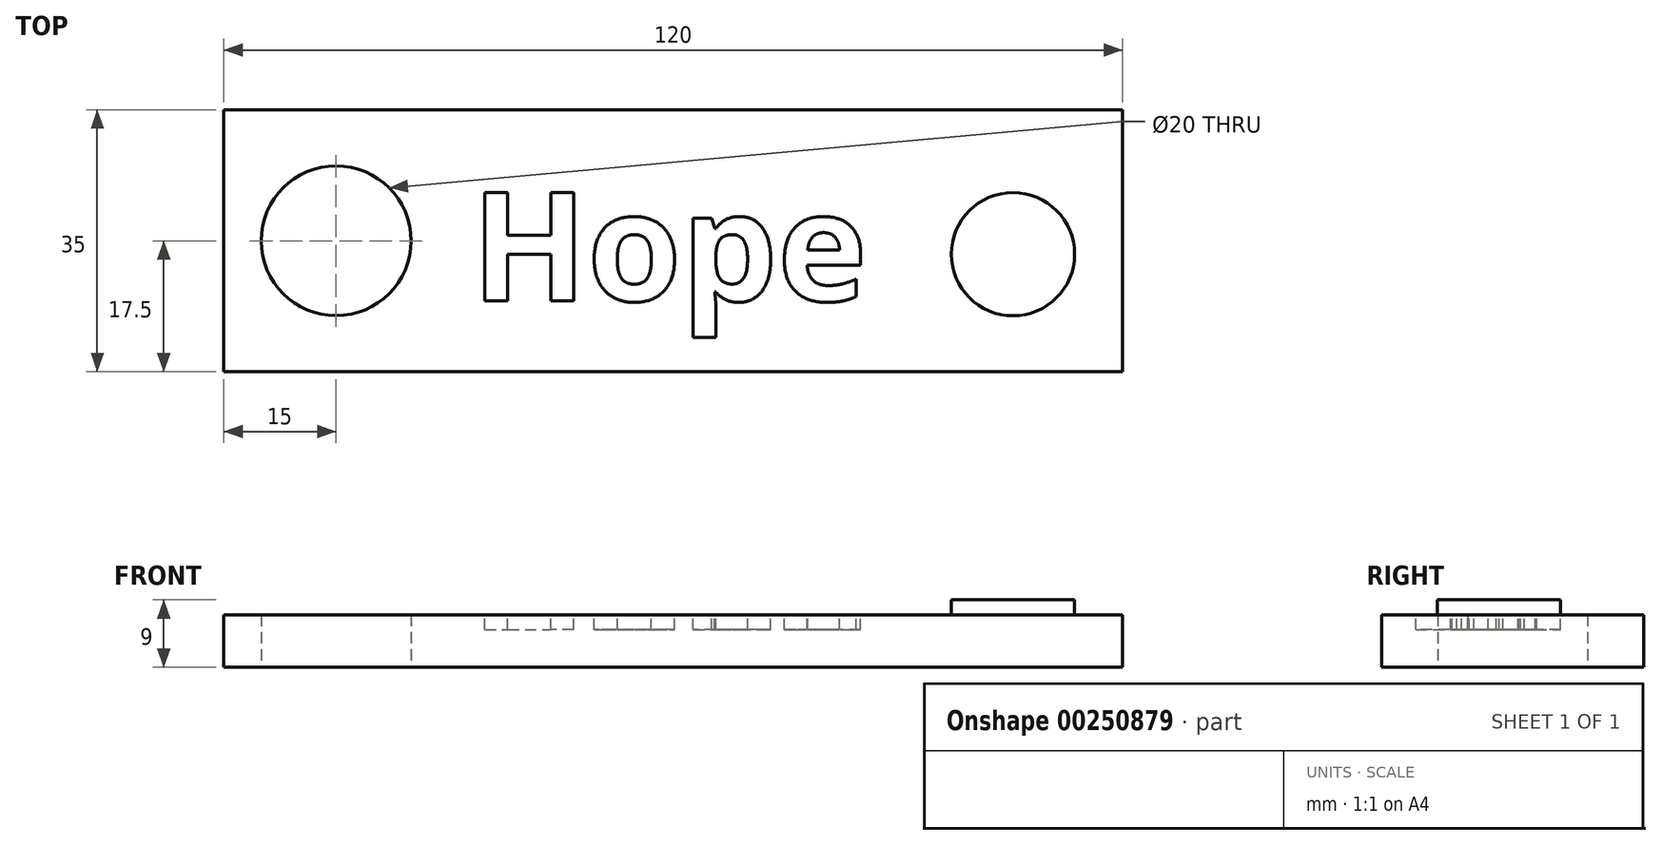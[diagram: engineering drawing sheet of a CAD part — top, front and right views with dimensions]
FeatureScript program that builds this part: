
annotation { "Feature Type Name" : "Feature", "Feature Type Description" : "" }
export const myFeature = defineFeature(function(context is Context, id is Id, definition is map)
    precondition{}
    {
        {
            var Q0;
            Q0=qCreatedBy(makeId("Top.planeOp"),FACE);
            var sketch = newSketch(context, id + "F0", { "sketchPlane" : qUnion([Q0])});
            skLineSegment(sketch, "E0.bottom", {"start": v(60, -17.5) * mm, "end": v(-60, -17.5) * mm});
            skLineSegment(sketch, "E0.top", {"start": v(60, 17.5) * mm, "end": v(-60, 17.5) * mm});
            skLineSegment(sketch, "E0.left", {"start": v(60, -17.5) * mm, "end": v(60, 17.5) * mm});
            skLineSegment(sketch, "E0.right", {"start": v(-60, -17.5) * mm, "end": v(-60, 17.5) * mm});
            skPoint(sketch, "E0.middle", {"position": v(0, 0) * mm});
            skCircle(sketch, "E1", {"center": v(-45, 0) * mm, "radius": 10 * mm});
            skSolve(sketch);
        }
        {
            var Q0;
            Q0=makeQuery(id+"F0.imprint","IMPRINT",FACE,{"disambiguationData":[TD([[makeQuery(id+"F0.imprint","IMPRINT",EDGE,{"derivedFrom":sQuery(id+"F0.wireOp",EDGE,"E0.bottom")}),-1.0]])]});
            var Q1;
            Q1=makeQuery(id+"FlfnzI0YaSvKUO7_0.imprint","IMPRINT",FACE,{"disambiguationData":[TD([[makeQuery(id+"FlfnzI0YaSvKUO7_0.imprint","IMPRINT",EDGE,{"derivedFrom":makeQuery(id+"F0.imprint","IMPRINT",EDGE,{"derivedFrom":sQuery(id+"F0.wireOp",EDGE,"E0.bottom")})}),-1.0]])]});
            var Q2;
            Q2=makeQuery(id+"Ff4yUPz2p8ofiq0_0.imprint","IMPRINT",FACE,{"disambiguationData":[TD([[makeQuery(id+"Ff4yUPz2p8ofiq0_0.imprint","IMPRINT",EDGE,{"derivedFrom":sQuery(id+"Ff4yUPz2p8ofiq0_0.wireOp",EDGE,"aaarCV0M-cDS9-31Ra-4nug-rVjWxFzt04Q0")}),-1.0]])]});
            extrude(context, id + "F1", {"entities" : qUnion([Q0, Q1, Q2]), "depth" : 7 * mm});
        }
        {
            var Q0;
            Q0=makeQuery(id+"F1.opExtrude","CAP_FACE",FACE,{"disambiguationData":[OSD([sQuery(id+"F0.wireOp",EDGE,"E0.bottom"),sQuery(id+"F0.wireOp",EDGE,"E0.top"),sQuery(id+"F0.wireOp",EDGE,"E0.left"),sQuery(id+"F0.wireOp",EDGE,"E0.right"),sQuery(id+"F0.wireOp",EDGE,"E1")])],"isStart":false});
            var sketch = newSketch(context, id + "F2", { "sketchPlane" : qUnion([Q0])});
            skText(sketch, "E2", { "text": "Hope", "fontName": "OpenSans-Bold.ttf"});
            const initialGuessF2  = {"E2": [-0.02697, -0.00804, 1, 0, 0.0146]};
            skSetInitialGuess(sketch, initialGuessF2);
            skSolve(sketch);
        }
        {
            var Q0;
            Q0 = qSketchRegion(id + "F2", true);
            extrude(context, id + "F3", {"entities" : qUnion([Q0]), "operationType" : NewBodyOperationType.REMOVE, "oppositeDirection" : true, "depth" : 2 * mm});
        }
        {
            var Q0;
            {var subQ0=sQuery(id+"F0.wireOp",EDGE,"E1");var subQ1=sQuery(id+"F0.wireOp",EDGE,"E0.top");var subQ2=sQuery(id+"F0.wireOp",EDGE,"E0.right");var subQ3=sQuery(id+"F0.wireOp",EDGE,"E0.bottom");var subQ4=sQuery(id+"F0.wireOp",EDGE,"E0.left");Q0=makeQuery(id+"F3.boolean.opBoolean","SPLIT",FACE,{"disambiguationData":[TD([makeQuery(id+"F1.opExtrude","SWEPT_FACE",FACE,{"disambiguationData":[OSD([subQ3])]})])],"derivedFrom":makeQuery(id+"F1.opExtrude","CAP_FACE",FACE,{"disambiguationData":[OSD([subQ3,subQ1,subQ4,subQ2,subQ0])],"isStart":false})});}
            var sketch = newSketch(context, id + "F4", { "sketchPlane" : qUnion([Q0])});
            skCircle(sketch, "E3", {"center": v(45.38, -1.8) * mm, "radius": 8.23 * mm});
            skSolve(sketch);
        }
        {
            var Q0;
            Q0=makeQuery(id+"F4.imprint","IMPRINT",FACE,{"disambiguationData":[TD([[makeQuery(id+"F4.imprint","IMPRINT",EDGE,{"derivedFrom":sQuery(id+"F4.wireOp",EDGE,"E3")}),1.0]])]});
            extrude(context, id + "F5", {"entities" : qUnion([Q0]), "operationType" : NewBodyOperationType.ADD, "depth" : 2 * mm});
        }
    });
